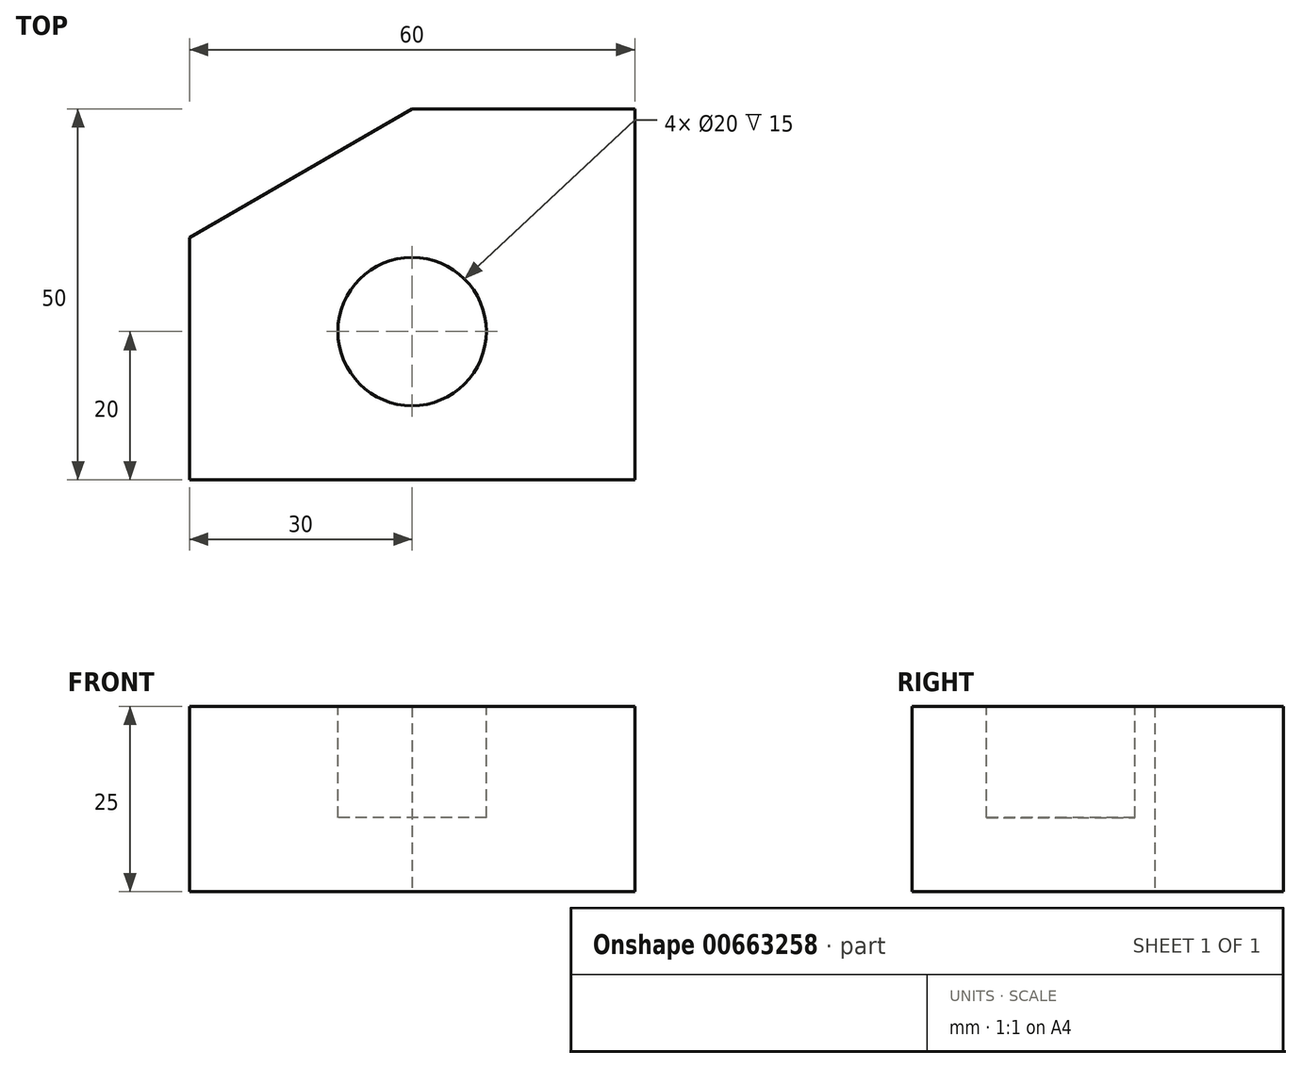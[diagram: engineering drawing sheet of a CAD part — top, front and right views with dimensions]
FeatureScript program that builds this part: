
annotation { "Feature Type Name" : "Feature", "Feature Type Description" : "" }
export const myFeature = defineFeature(function(context is Context, id is Id, definition is map)
    precondition{}
    {
        {
            var Q0;
            Q0=qCreatedBy(makeId("Top.planeOp"),FACE);
            var sketch = newSketch(context, id + "F0", { "sketchPlane" : qUnion([Q0])});
            skLineSegment(sketch, "E0", {"start": v(0, 0) * mm, "end": v(0, 32.68) * mm});
            skLineSegment(sketch, "E1", {"start": v(0, 32.68) * mm, "end": v(30, 50) * mm});
            skLineSegment(sketch, "E2", {"start": v(30, 50) * mm, "end": v(60, 50) * mm});
            skLineSegment(sketch, "E3", {"start": v(60, 50) * mm, "end": v(60, 0) * mm});
            skLineSegment(sketch, "E4", {"start": v(60, 0) * mm, "end": v(0, 0) * mm});
            skSolve(sketch);
        }
        {
            var Q0;
            Q0 = qSketchRegion(id + "F0", true);
            extrude(context, id + "F1", {"entities" : qUnion([Q0]), "depth" : 25 * mm, "offsetDistance" : 25 * mm});
        }
        {
            var Q0;
            Q0=makeQuery(id+"F1.opExtrude","CAP_FACE",FACE,{"disambiguationData":[OSD([sQuery(id+"F0.wireOp",EDGE,"E0"),sQuery(id+"F0.wireOp",EDGE,"E1"),sQuery(id+"F0.wireOp",EDGE,"E2"),sQuery(id+"F0.wireOp",EDGE,"E3"),sQuery(id+"F0.wireOp",EDGE,"E4")])],"isStart":false});
            var sketch = newSketch(context, id + "F2", { "sketchPlane" : qUnion([Q0])});
            skCircle(sketch, "E5", {"center": v(30, 20) * mm, "radius": 10 * mm});
            skSolve(sketch);
        }
        {
            var Q0;
            Q0 = qSketchRegion(id + "F2", true);
            extrude(context, id + "F3", {"entities" : qUnion([Q0]), "operationType" : NewBodyOperationType.REMOVE, "oppositeDirection" : true, "depth" : 15 * mm, "offsetDistance" : 25 * mm});
        }
    });
